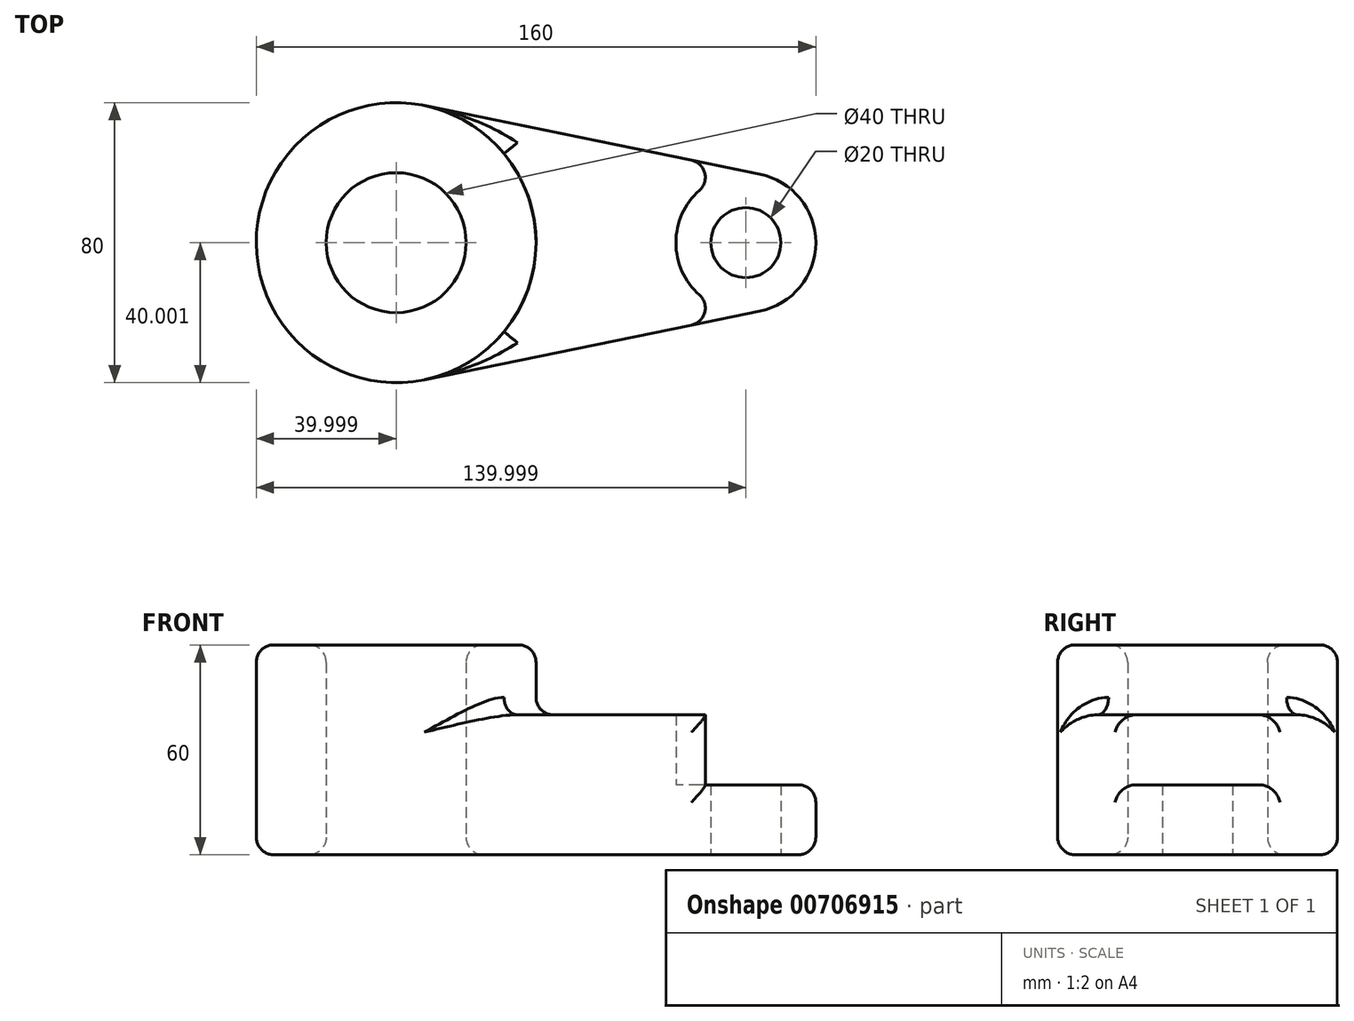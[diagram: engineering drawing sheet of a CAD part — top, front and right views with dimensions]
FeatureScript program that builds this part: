
annotation { "Feature Type Name" : "Feature", "Feature Type Description" : "" }
export const myFeature = defineFeature(function(context is Context, id is Id, definition is map)
    precondition{}
    {
        {
            var Q0;
            Q0=qCreatedBy(makeId("Top.planeOp"),FACE);
            var sketch = newSketch(context, id + "F0", { "sketchPlane" : qUnion([Q0])});
            skCircle(sketch, "E0", {"center": v(-55.4, -3.8) * mm, "radius": 40 * mm});
            skCircle(sketch, "E1", {"center": v(-55.4, -3.8) * mm, "radius": 20 * mm});
            skCircle(sketch, "E2", {"center": v(44.6, -3.8) * mm, "radius": 10 * mm});
            skCircle(sketch, "E3", {"center": v(44.6, -3.8) * mm, "radius": 20 * mm});
            skLineSegment(sketch, "E4", {"start": v(-47.4, 35.38) * mm, "end": v(48.6, 15.79) * mm});
            skLineSegment(sketch, "E5", {"start": v(-47.4, -43) * mm, "end": v(48.6, -23.4) * mm});
            skSolve(sketch);
        }
        {
            var Q0;
            Q0=makeQuery(id+"F0.imprint","IMPRINT",FACE,{"disambiguationData":[TD([[makeQuery(id+"F0.imprint","IMPRINT",EDGE,{"derivedFrom":sQuery(id+"F0.wireOp",EDGE,"E1")}),-1.0]])]});
            extrude(context, id + "F1", {"entities" : qUnion([Q0]), "depth" : 60 * mm, "offsetDistance" : 25 * mm});
        }
        {
            var Q0;
            {var subQ0=sQuery(id+"F0.wireOp",EDGE,"E4");Q0=makeQuery(id+"F0.imprint","IMPRINT",FACE,{"disambiguationData":[TD([[makeQuery(id+"F0.imprint","IMPRINT",EDGE,{"derivedFrom":subQ0}),-1.0]])]});}
            extrude(context, id + "F2", {"entities" : qUnion([Q0]), "operationType" : NewBodyOperationType.ADD, "depth" : 40 * mm, "offsetDistance" : 25 * mm});
        }
        {
            var Q0;
            Q0=makeQuery(id+"F0.imprint","IMPRINT",FACE,{"disambiguationData":[TD([[makeQuery(id+"F0.imprint","IMPRINT",EDGE,{"derivedFrom":sQuery(id+"F0.wireOp",EDGE,"E2")}),-1.0]])]});
            extrude(context, id + "F3", {"entities" : qUnion([Q0]), "operationType" : NewBodyOperationType.ADD, "depth" : 20 * mm, "offsetDistance" : 25 * mm});
        }
        {
            var Q0;
            Q0=makeQuery(id+"F2.opExtrude","SWEPT_FACE",FACE,{"disambiguationData":[OSD([sQuery(id+"F0.wireOp",EDGE,"E4")])]});
            fillet(context, id + "F4", {"entities" : qUnion([Q0]), "radius" : 5 * mm, "tangentPropagation" : true, "allowEdgeOverflow" : false});
        }
        {
            var Q0;
            Q0=makeQuery(id+"F2.opExtrude","SWEPT_FACE",FACE,{"disambiguationData":[OSD([sQuery(id+"F0.wireOp",EDGE,"E5")])]});
            var Q1;
            Q1=makeQuery(id+"F1.opExtrude","CAP_FACE",FACE,{"disambiguationData":[OSD([sQuery(id+"F0.wireOp",EDGE,"E0"),sQuery(id+"F0.wireOp",EDGE,"E1")])],"isStart":false});
            var Q2;
            Q2=makeQuery(id+"F1.opExtrude","SWEPT_FACE",FACE,{"disambiguationData":[OSD([sQuery(id+"F0.wireOp",EDGE,"E1")])]});
            var Q3;
            Q3=makeQuery(id+"F1.opExtrude","SWEPT_FACE",FACE,{"disambiguationData":[OSD([sQuery(id+"F0.wireOp",EDGE,"E0")])]});
            fillet(context, id + "F5", {"entities" : qUnion([Q0, Q1, Q2, Q3]), "radius" : 5 * mm, "tangentPropagation" : true, "allowEdgeOverflow" : false});
        }
        {
            var Q0;
            {var subQ0=sQuery(id+"F0.wireOp",EDGE,"E3");Q0=makeQuery(id+"F3.boolean.opBoolean","SPLIT",EDGE,{"disambiguationData":[topologyDisambiguationEdgeConnected([makeQuery(id+"F3.opExtrude","SWEPT_FACE",FACE,{"disambiguationData":[OSD([subQ0])]})])],"derivedFrom":makeQuery(id+"F3.opExtrude","CAP_EDGE",EDGE,{"disambiguationData":[OSD([subQ0])],"isStart":false})});}
            fillet(context, id + "F6", {"entities" : qUnion([Q0]), "radius" : 5 * mm, "tangentPropagation" : true, "allowEdgeOverflow" : false});
        }
    });
